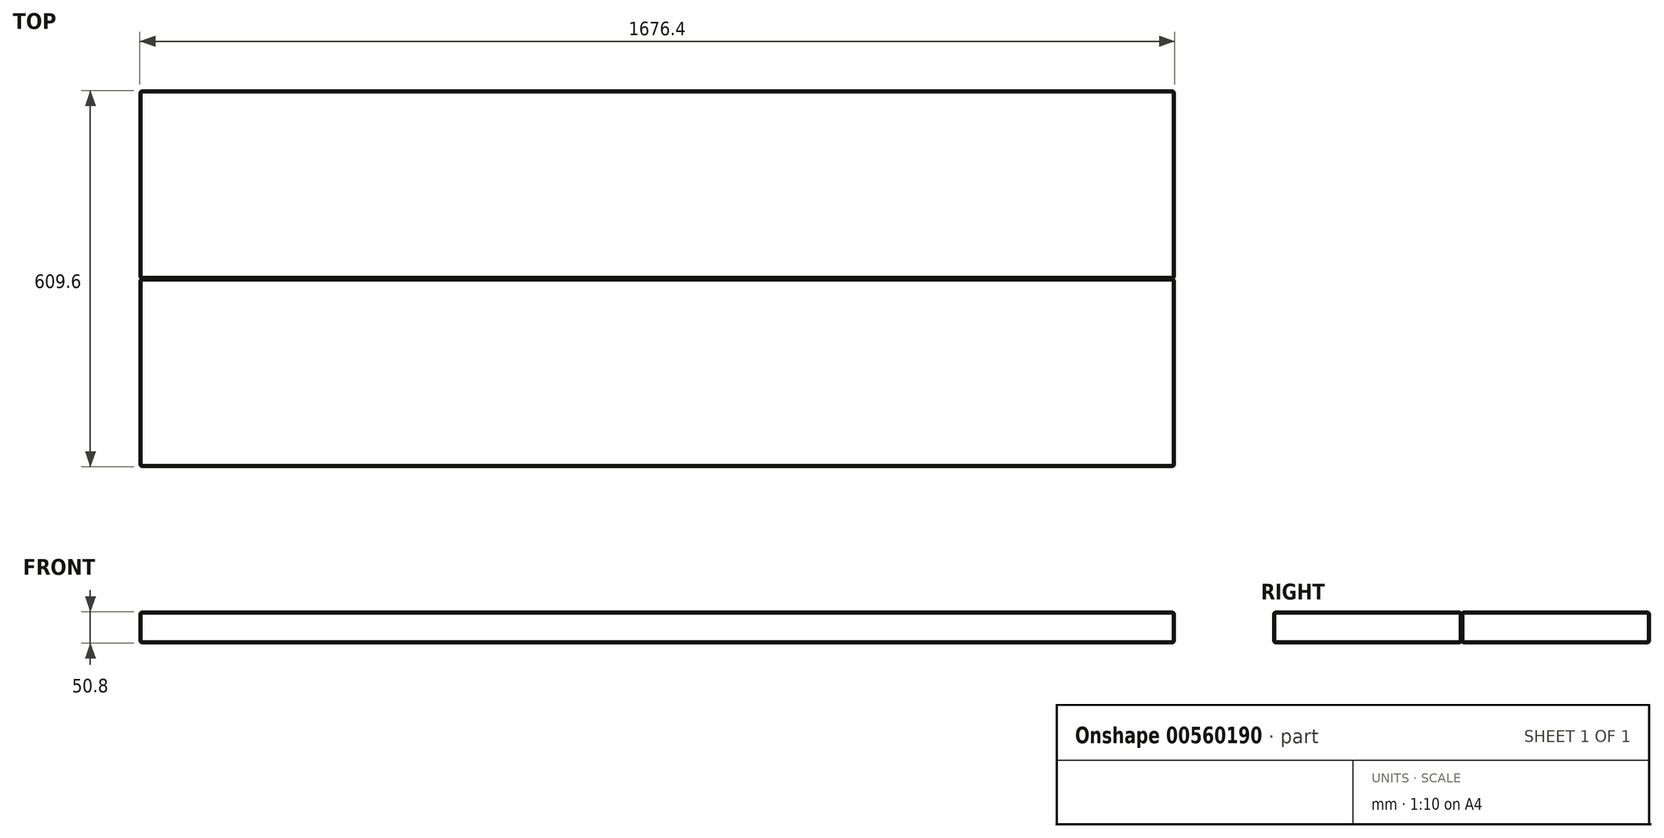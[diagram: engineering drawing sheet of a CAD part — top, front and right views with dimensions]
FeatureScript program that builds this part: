
annotation { "Feature Type Name" : "Feature", "Feature Type Description" : "" }
export const myFeature = defineFeature(function(context is Context, id is Id, definition is map)
    precondition{}
    {
        {
            var Q0;
            Q0=qCreatedBy(makeId("Top.planeOp"),FACE);
            var sketch = newSketch(context, id + "F0", { "sketchPlane" : qUnion([Q0])});
            skLineSegment(sketch, "E0", {"start": v(0, 0) * mm, "end": v(0, 198.89) * mm, "construction": true});
            skLineSegment(sketch, "E1", {"start": v(0, 0) * mm, "end": v(955.94, 0) * mm, "construction": true});
            skLineSegment(sketch, "E2.bottom", {"start": v(838.2, 0) * mm, "end": v(-838.2, 0) * mm});
            skLineSegment(sketch, "E2.top", {"start": v(838.2, -304.8) * mm, "end": v(-838.2, -304.8) * mm});
            skLineSegment(sketch, "E2.left", {"start": v(838.2, 0) * mm, "end": v(838.2, -304.8) * mm});
            skLineSegment(sketch, "E2.right", {"start": v(-838.2, 0) * mm, "end": v(-838.2, -304.8) * mm});
            skSolve(sketch);
        }
        {
            var Q0;
            Q0=makeQuery(id+"F0.imprint","IMPRINT",FACE,{"disambiguationData":[TD([[makeQuery(id+"F0.imprint","IMPRINT",EDGE,{"derivedFrom":sQuery(id+"F0.wireOp",EDGE,"E2.bottom")}),1.0]])]});
            extrude(context, id + "F1", {"entities" : qUnion([Q0]), "depth" : 50.8 * mm, "offsetDistance" : 25.4 * mm});
        }
        {
            var Q0;
            Q0=makeQuery(id+"F1.opExtrude","CAP_FACE",FACE,{"disambiguationData":[OSD([sQuery(id+"F0.wireOp",EDGE,"E2.bottom"),sQuery(id+"F0.wireOp",EDGE,"E2.top"),sQuery(id+"F0.wireOp",EDGE,"E2.left"),sQuery(id+"F0.wireOp",EDGE,"E2.right")])],"isStart":false});
            var Q1;
            Q1=makeQuery(id+"F1.opExtrude","SWEPT_FACE",FACE,{"disambiguationData":[OSD([sQuery(id+"F0.wireOp",EDGE,"E2.top")])]});
            var Q2;
            Q2=makeQuery(id+"F1.opExtrude","CAP_EDGE",EDGE,{"disambiguationData":[OSD([sQuery(id+"F0.wireOp",EDGE,"E2.left")])],"isStart":true});
            var Q3;
            Q3=makeQuery(id+"F1.opExtrude","SWEPT_FACE",FACE,{"disambiguationData":[OSD([sQuery(id+"F0.wireOp",EDGE,"E2.right")])]});
            var Q4;
            Q4=makeQuery(id+"F1.opExtrude","SWEPT_FACE",FACE,{"disambiguationData":[OSD([sQuery(id+"F0.wireOp",EDGE,"E2.bottom")])]});
            var Q5;
            Q5=makeQuery(id+"F1.opExtrude","CAP_FACE",FACE,{"disambiguationData":[OSD([sQuery(id+"F0.wireOp",EDGE,"E2.bottom"),sQuery(id+"F0.wireOp",EDGE,"E2.top"),sQuery(id+"F0.wireOp",EDGE,"E2.left"),sQuery(id+"F0.wireOp",EDGE,"E2.right")])],"isStart":true});
            chamfer(context, id + "F2", {"entities" : qUnion([Q0, Q1, Q2, Q3, Q4, Q5]), "width" : 2.54 * mm, "tangentPropagation" : true});
        }
        {
            var Q0;
            Q0=makeQuery(id+"F1.opExtrude","SWEPT_BODY",BODY,{"disambiguationData":[OSD([sQuery(id+"F0.wireOp",EDGE,"E2.bottom"),sQuery(id+"F0.wireOp",EDGE,"E2.top"),sQuery(id+"F0.wireOp",EDGE,"E2.left"),sQuery(id+"F0.wireOp",EDGE,"E2.right")])]});
            var Q1;
            Q1=qCreatedBy(makeId("Front.planeOp"),FACE);
            mirror(context, id + "F3", {"operationType" : NewBodyOperationType.ADD, "entities" : qUnion([Q0]), "mirrorPlane" : qUnion([Q1])});
        }
        {
            var Q0;
            Q0=makeQuery(id+"F1.opExtrude","CAP_FACE",FACE,{"disambiguationData":[OSD([sQuery(id+"F0.wireOp",EDGE,"E2.bottom"),sQuery(id+"F0.wireOp",EDGE,"E2.top"),sQuery(id+"F0.wireOp",EDGE,"E2.left"),sQuery(id+"F0.wireOp",EDGE,"E2.right")])],"isStart":true});
            var sketch = newSketch(context, id + "F4", { "sketchPlane" : qUnion([Q0])});
            skLineSegment(sketch, "E3.bottom", {"start": v(-628.97, 191.14) * mm, "end": v(628.97, 191.14) * mm, "construction": true});
            skLineSegment(sketch, "E3.top", {"start": v(-628.97, -191.14) * mm, "end": v(628.97, -191.14) * mm, "construction": true});
            skLineSegment(sketch, "E3.left", {"start": v(-628.97, 191.14) * mm, "end": v(-628.97, -191.14) * mm, "construction": true});
            skLineSegment(sketch, "E3.right", {"start": v(628.97, 191.14) * mm, "end": v(628.97, -191.14) * mm, "construction": true});
            skLineSegment(sketch, "E4", {"start": v(0, 0) * mm, "end": v(0, 191.14) * mm, "construction": true});
            skLineSegment(sketch, "E5", {"start": v(0, 0) * mm, "end": v(628.97, 0) * mm, "construction": true});
            skSolve(sketch);
        }
    });
